# Revit family: SP4180W_Revit
name_source: partatom
category: Mechanical Equipment
revit_build: Autodesk Revit 2014 (Build: 20130215_1615(x64)
units: mm (PartAtom-declared; Revit-internal decimal feet)

## types (1)
- Standard
    Connector_10_Diameter = 0' - 0"
    Connector_11_Diameter = 0' - 0"
    Connector_3_Diameter = 0' - 0"
    Connector_4_Diameter = 0' - 0"
    Connector_5_Diameter = 0' - 0"
    Connector_6_Diameter = 0' - 0"
    Connector_7_Diameter = 0' - 0"
    Connector_8_Diameter = 0' - 0"
    Connector_9_Diameter = 0' - 0"
    Description = Electric Resistive humidifier Weather proof
    Design Status = 1
    Extrusion_End_1 = 0' - 0"
    Extrusion_End_2 = 0' - 0"
    Manufacturer = Neptronic
    Model = SK302-W, SK304-W, SK306-W
    Part Number = SP4180W_Shrinkwrap_test
    URL = www.neptronic.com
    d104 = 0' - 0 1/4"
    d106 = 0' - 0 1/4"
    d108 = 0' - 0 1/4"
    d110 = 0' - 0 1/4"
    d112 = 0' - 0 1/4"
    d114 = 0' - 0 1/4"
    d116 = 0' - 1 13/32"
    d118 = 0' - 1 13/32"
    d124 = 0' - 0 9/32"
    d126 = 1' - 10 13/32"
    d128 = 2' - 4 15/32"
    d130 = 2' - 1 3/4"
    d132 = 0' - 0"
    d134 = 0' - 0"
    d136 = 0' - 0"

## geometry (parser evidence)
native form markers: Extrusion x2, Sweep x1
no freeform markers — native parametric forms only
